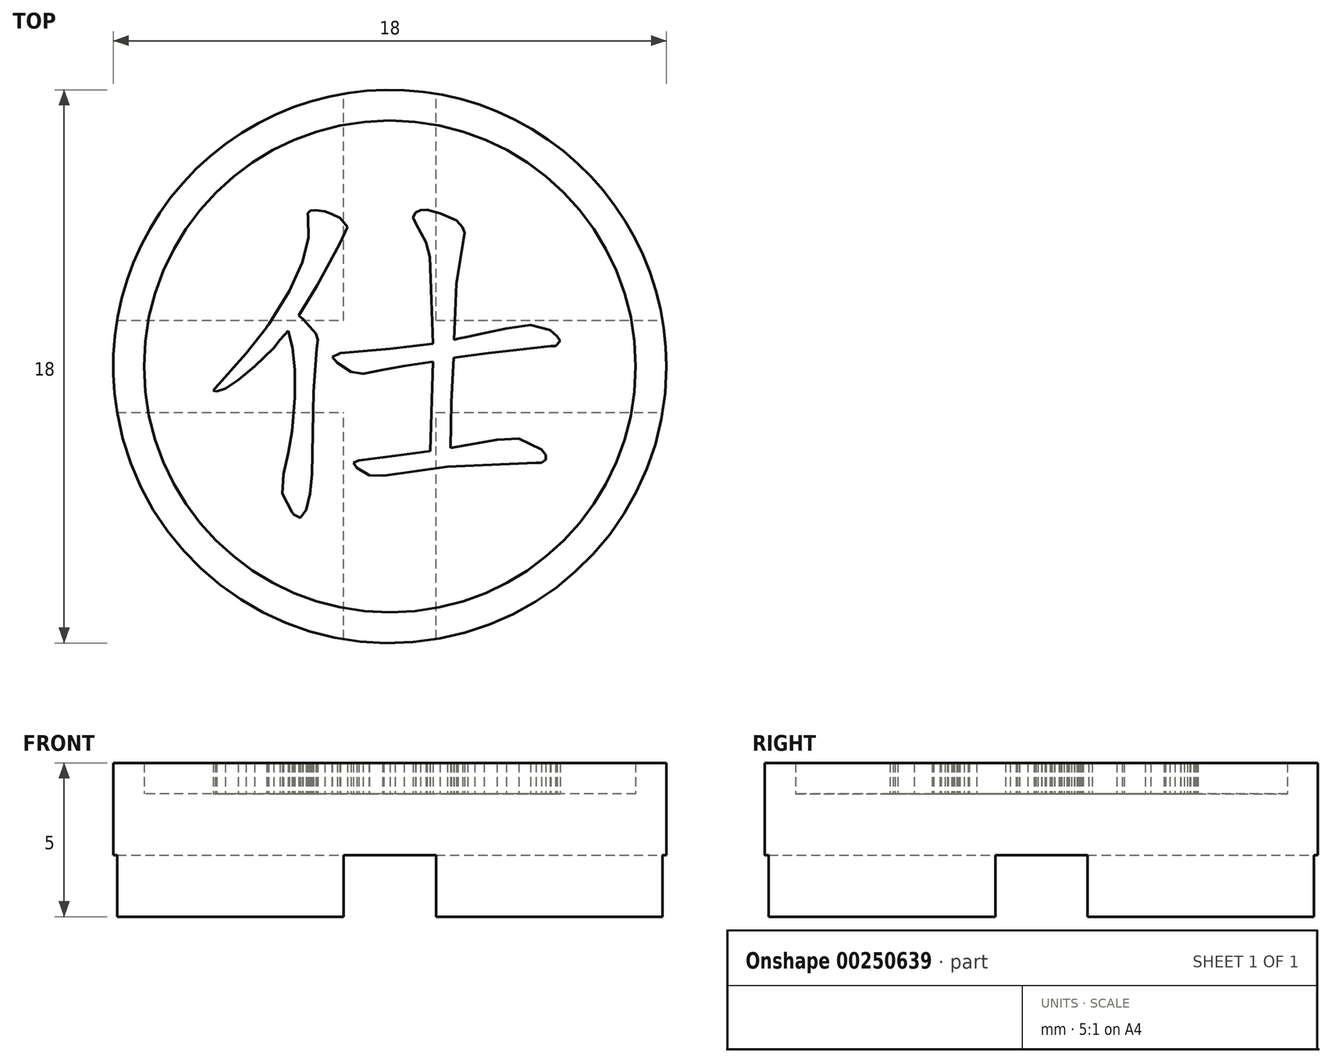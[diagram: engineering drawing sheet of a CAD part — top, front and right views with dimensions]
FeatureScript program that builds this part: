
annotation { "Feature Type Name" : "Feature", "Feature Type Description" : "" }
export const myFeature = defineFeature(function(context is Context, id is Id, definition is map)
    precondition{}
    {
        {
            var Q0;
            Q0=qCreatedBy(makeId("Top.planeOp"),FACE);
            var sketch = newSketch(context, id + "F0", { "sketchPlane" : qUnion([Q0])});
            skCircle(sketch, "E0", {"center": v(-31.33, 19.76) * mm, "radius": 9 * mm});
            skSolve(sketch);
        }
        {
            var Q0;
            Q0=qSketchRegion(id+"F0",true);
            extrude(context, id + "F1", {"entities" : qUnion([Q0]), "depth" : 4 * mm});
        }
        {
            var Q0;
            Q0=makeQuery(id+"F1.opExtrude","CAP_FACE",FACE,{"disambiguationData":[OSD([sQuery(id+"F0.wireOp",EDGE,"E0")])],"isStart":false});
            var sketch = newSketch(context, id + "F2", { "sketchPlane" : qUnion([Q0])});
            skCircle(sketch, "E1", {"center": v(-31.33, 19.76) * mm, "radius": 8 * mm});
            skCircle(sketch, "E2", {"center": v(-31.33, 19.76) * mm, "radius": 9 * mm});
            skSolve(sketch);
        }
        {
            var Q0;
            Q0=makeQuery(id+"F1.opExtrude","CAP_FACE",FACE,{"disambiguationData":[OSD([sQuery(id+"F0.wireOp",EDGE,"E0")])],"isStart":true});
            var sketch = newSketch(context, id + "F3", { "sketchPlane" : qUnion([Q0])});
            skLineSegment(sketch, "E3", {"start": v(-31.33, -19.76) * mm, "end": v(-22.33, -19.76) * mm, "construction": true});
            skLineSegment(sketch, "E4", {"start": v(-31.33, -19.76) * mm, "end": v(-31.33, -10.76) * mm, "construction": true});
            skLineSegment(sketch, "E5", {"start": v(-31.33, -19.76) * mm, "end": v(-40.33, -19.76) * mm, "construction": true});
            skLineSegment(sketch, "E6", {"start": v(-31.33, -19.76) * mm, "end": v(-31.33, -28.76) * mm, "construction": true});
            skLineSegment(sketch, "E7.bottom", {"start": v(-40.33, -28.76) * mm, "end": v(-22.33, -28.76) * mm});
            skLineSegment(sketch, "E7.top", {"start": v(-40.33, -10.76) * mm, "end": v(-22.33, -10.76) * mm});
            skLineSegment(sketch, "E7.left", {"start": v(-22.33, -10.76) * mm, "end": v(-22.33, -28.76) * mm});
            skLineSegment(sketch, "E7.right", {"start": v(-40.33, -10.76) * mm, "end": v(-40.33, -28.76) * mm});
            skPoint(sketch, "E8", {"position": v(-31.33, -28.76) * mm});
            skPoint(sketch, "E9", {"position": v(-40.33, -19.76) * mm});
            skPoint(sketch, "E10", {"position": v(-22.33, -19.76) * mm});
            skPoint(sketch, "E11", {"position": v(-31.33, -10.76) * mm});
            skLineSegment(sketch, "E12.bottom", {"start": v(-32.83, -10.76) * mm, "end": v(-29.83, -10.76) * mm});
            skLineSegment(sketch, "E12.top", {"start": v(-32.83, -28.76) * mm, "end": v(-29.83, -28.76) * mm});
            skLineSegment(sketch, "E12.left", {"start": v(-32.83, -10.76) * mm, "end": v(-32.83, -28.76) * mm});
            skLineSegment(sketch, "E12.right", {"start": v(-29.83, -10.76) * mm, "end": v(-29.83, -28.76) * mm});
            skLineSegment(sketch, "E13.bottom", {"start": v(-40.33, -18.26) * mm, "end": v(-22.33, -18.26) * mm});
            skLineSegment(sketch, "E13.top", {"start": v(-40.33, -21.26) * mm, "end": v(-22.33, -21.26) * mm});
            skLineSegment(sketch, "E13.left", {"start": v(-40.33, -18.26) * mm, "end": v(-40.33, -21.26) * mm});
            skLineSegment(sketch, "E13.right", {"start": v(-22.33, -18.26) * mm, "end": v(-22.33, -21.26) * mm});
            skSolve(sketch);
        }
        {
            var Q0;
            {var subQ1=sQuery(id+"F3.wireOp",EDGE,"E12.bottom");var subQ3=makeQuery(id+"F1.opExtrude","CAP_EDGE",EDGE,{"disambiguationData":[OSD([sQuery(id+"F0.wireOp",EDGE,"E0")])],"isStart":true});var subQ4=makeQuery(id+"F3.imprint","INTERSECT",VERTEX,{"derivedFrom":[subQ3,subQ1]});Q0=makeQuery(id+"F3.imprint","IMPRINT",FACE,{"disambiguationData":[TD([[makeQuery(id+"F3.imprint","IMPRINT",EDGE,{"disambiguationData":[TD([[subQ4,1.0]])],"derivedFrom":subQ3}),1.0]])]});}
            var Q1;
            {var subQ1=sQuery(id+"F3.wireOp",EDGE,"E12.bottom");var subQ3=makeQuery(id+"F1.opExtrude","CAP_EDGE",EDGE,{"disambiguationData":[OSD([sQuery(id+"F0.wireOp",EDGE,"E0")])],"isStart":true});var subQ4=makeQuery(id+"F3.imprint","INTERSECT",VERTEX,{"derivedFrom":[subQ3,subQ1]});Q1=makeQuery(id+"F3.imprint","IMPRINT",FACE,{"disambiguationData":[TD([[makeQuery(id+"F3.imprint","IMPRINT",EDGE,{"disambiguationData":[TD([[subQ4,-1.0]])],"derivedFrom":subQ3}),1.0]])]});}
            var Q2;
            {var subQ1=sQuery(id+"F3.wireOp",EDGE,"E12.top");var subQ3=makeQuery(id+"F1.opExtrude","CAP_EDGE",EDGE,{"disambiguationData":[OSD([sQuery(id+"F0.wireOp",EDGE,"E0")])],"isStart":true});var subQ4=makeQuery(id+"F3.imprint","INTERSECT",VERTEX,{"derivedFrom":[subQ3,subQ1]});Q2=makeQuery(id+"F3.imprint","IMPRINT",FACE,{"disambiguationData":[TD([[makeQuery(id+"F3.imprint","IMPRINT",EDGE,{"disambiguationData":[TD([[subQ4,-1.0]])],"derivedFrom":subQ3}),1.0]])]});}
            var Q3;
            {var subQ1=sQuery(id+"F3.wireOp",EDGE,"E12.top");var subQ3=makeQuery(id+"F1.opExtrude","CAP_EDGE",EDGE,{"disambiguationData":[OSD([sQuery(id+"F0.wireOp",EDGE,"E0")])],"isStart":true});var subQ4=makeQuery(id+"F3.imprint","INTERSECT",VERTEX,{"derivedFrom":[subQ3,subQ1]});Q3=makeQuery(id+"F3.imprint","IMPRINT",FACE,{"disambiguationData":[TD([[makeQuery(id+"F3.imprint","IMPRINT",EDGE,{"disambiguationData":[TD([[subQ4,1.0]])],"derivedFrom":subQ3}),1.0]])]});}
            var Q4;
            {var subQ0=sQuery(id+"F3.wireOp",EDGE,"E13.left");var subQ3=makeQuery(id+"F1.opExtrude","CAP_EDGE",EDGE,{"disambiguationData":[OSD([sQuery(id+"F0.wireOp",EDGE,"E0")])],"isStart":true});var subQ5=makeQuery(id+"F3.imprint","INTERSECT",VERTEX,{"derivedFrom":[subQ3,subQ0]});Q4=makeQuery(id+"F3.imprint","IMPRINT",FACE,{"disambiguationData":[TD([[makeQuery(id+"F3.imprint","IMPRINT",EDGE,{"disambiguationData":[TD([[subQ5,-1.0]])],"derivedFrom":subQ3}),1.0]])]});}
            var Q5;
            {var subQ0=sQuery(id+"F3.wireOp",EDGE,"E13.right");var subQ3=makeQuery(id+"F1.opExtrude","CAP_EDGE",EDGE,{"disambiguationData":[OSD([sQuery(id+"F0.wireOp",EDGE,"E0")])],"isStart":true});var subQ5=makeQuery(id+"F3.imprint","INTERSECT",VERTEX,{"derivedFrom":[subQ3,subQ0]});Q5=makeQuery(id+"F3.imprint","IMPRINT",FACE,{"disambiguationData":[TD([[makeQuery(id+"F3.imprint","IMPRINT",EDGE,{"disambiguationData":[TD([[subQ5,1.0]])],"derivedFrom":subQ3}),1.0]])]});}
            var Q6;
            {var subQ0=sQuery(id+"F3.wireOp",EDGE,"E13.left");var subQ3=makeQuery(id+"F1.opExtrude","CAP_EDGE",EDGE,{"disambiguationData":[OSD([sQuery(id+"F0.wireOp",EDGE,"E0")])],"isStart":true});var subQ5=makeQuery(id+"F3.imprint","INTERSECT",VERTEX,{"derivedFrom":[subQ3,subQ0]});Q6=makeQuery(id+"F3.imprint","IMPRINT",FACE,{"disambiguationData":[TD([[makeQuery(id+"F3.imprint","IMPRINT",EDGE,{"disambiguationData":[TD([[subQ5,1.0]])],"derivedFrom":subQ3}),1.0]])]});}
            var Q7;
            {var subQ0=sQuery(id+"F3.wireOp",EDGE,"E13.right");var subQ3=makeQuery(id+"F1.opExtrude","CAP_EDGE",EDGE,{"disambiguationData":[OSD([sQuery(id+"F0.wireOp",EDGE,"E0")])],"isStart":true});var subQ5=makeQuery(id+"F3.imprint","INTERSECT",VERTEX,{"derivedFrom":[subQ3,subQ0]});Q7=makeQuery(id+"F3.imprint","IMPRINT",FACE,{"disambiguationData":[TD([[makeQuery(id+"F3.imprint","IMPRINT",EDGE,{"disambiguationData":[TD([[subQ5,-1.0]])],"derivedFrom":subQ3}),1.0]])]});}
            var Q8;
            {var subQ3=makeQuery(id+"F1.opExtrude","CAP_EDGE",EDGE,{"disambiguationData":[OSD([sQuery(id+"F0.wireOp",EDGE,"E0")])],"isStart":true});var subQ5=sQuery(id+"F3.wireOp",EDGE,"E12.left");var subQ8=makeQuery(id+"F3.imprint","INTERSECT",VERTEX,{"disambiguationData":[OD(1.0)],"derivedFrom":[subQ3,subQ5]});Q8=makeQuery(id+"F3.imprint","IMPRINT",FACE,{"disambiguationData":[TD([[makeQuery(id+"F3.imprint","IMPRINT",EDGE,{"disambiguationData":[TD([[subQ8,-1.0]])],"derivedFrom":subQ3}),1.0]])]});}
            var Q9;
            {var subQ3=makeQuery(id+"F1.opExtrude","CAP_EDGE",EDGE,{"disambiguationData":[OSD([sQuery(id+"F0.wireOp",EDGE,"E0")])],"isStart":true});var subQ5=sQuery(id+"F3.wireOp",EDGE,"E12.right");var subQ8=makeQuery(id+"F3.imprint","INTERSECT",VERTEX,{"disambiguationData":[OD(1.0)],"derivedFrom":[subQ3,subQ5]});Q9=makeQuery(id+"F3.imprint","IMPRINT",FACE,{"disambiguationData":[TD([[makeQuery(id+"F3.imprint","IMPRINT",EDGE,{"disambiguationData":[TD([[subQ8,1.0]])],"derivedFrom":subQ3}),1.0]])]});}
            var Q10;
            {var subQ3=makeQuery(id+"F1.opExtrude","CAP_EDGE",EDGE,{"disambiguationData":[OSD([sQuery(id+"F0.wireOp",EDGE,"E0")])],"isStart":true});var subQ5=sQuery(id+"F3.wireOp",EDGE,"E12.left");var subQ8=makeQuery(id+"F3.imprint","INTERSECT",VERTEX,{"disambiguationData":[OD(0.0)],"derivedFrom":[subQ3,subQ5]});Q10=makeQuery(id+"F3.imprint","IMPRINT",FACE,{"disambiguationData":[TD([[makeQuery(id+"F3.imprint","IMPRINT",EDGE,{"disambiguationData":[TD([[subQ8,1.0]])],"derivedFrom":subQ3}),1.0]])]});}
            var Q11;
            {var subQ3=makeQuery(id+"F1.opExtrude","CAP_EDGE",EDGE,{"disambiguationData":[OSD([sQuery(id+"F0.wireOp",EDGE,"E0")])],"isStart":true});var subQ5=sQuery(id+"F3.wireOp",EDGE,"E12.right");var subQ8=makeQuery(id+"F3.imprint","INTERSECT",VERTEX,{"disambiguationData":[OD(0.0)],"derivedFrom":[subQ3,subQ5]});Q11=makeQuery(id+"F3.imprint","IMPRINT",FACE,{"disambiguationData":[TD([[makeQuery(id+"F3.imprint","IMPRINT",EDGE,{"disambiguationData":[TD([[subQ8,-1.0]])],"derivedFrom":subQ3}),1.0]])]});}
            var Q12;
            {var subQ2=sQuery(id+"F3.wireOp",EDGE,"E12.left");var subQ4=sQuery(id+"F3.wireOp",EDGE,"E13.bottom");var subQ8=makeQuery(id+"F3.imprint","INTERSECT",VERTEX,{"derivedFrom":[subQ2,subQ4]});Q12=makeQuery(id+"F3.imprint","IMPRINT",FACE,{"disambiguationData":[TD([[makeQuery(id+"F3.imprint","IMPRINT",EDGE,{"disambiguationData":[TD([[subQ8,1.0]])],"derivedFrom":subQ2}),1.0]])]});}
            var Q13;
            {var subQ1=sQuery(id+"F3.wireOp",EDGE,"E12.left");var subQ5=sQuery(id+"F3.wireOp",EDGE,"E13.bottom");var subQ6=makeQuery(id+"F3.imprint","INTERSECT",VERTEX,{"derivedFrom":[subQ1,subQ5]});Q13=makeQuery(id+"F3.imprint","IMPRINT",FACE,{"disambiguationData":[TD([[makeQuery(id+"F3.imprint","IMPRINT",EDGE,{"disambiguationData":[TD([[subQ6,-1.0]])],"derivedFrom":subQ1}),-1.0]])]});}
            var Q14;
            {var subQ0=sQuery(id+"F3.wireOp",EDGE,"E13.top");var subQ1=sQuery(id+"F3.wireOp",EDGE,"E12.left");var subQ2=makeQuery(id+"F3.imprint","INTERSECT",VERTEX,{"derivedFrom":[subQ1,subQ0]});Q14=makeQuery(id+"F3.imprint","IMPRINT",FACE,{"disambiguationData":[TD([[makeQuery(id+"F3.imprint","IMPRINT",EDGE,{"disambiguationData":[TD([[subQ2,-1.0]])],"derivedFrom":subQ1}),1.0]])]});}
            var Q15;
            {var subQ2=sQuery(id+"F3.wireOp",EDGE,"E13.bottom");var subQ5=sQuery(id+"F3.wireOp",EDGE,"E12.right");var subQ8=makeQuery(id+"F3.imprint","INTERSECT",VERTEX,{"derivedFrom":[subQ5,subQ2]});Q15=makeQuery(id+"F3.imprint","IMPRINT",FACE,{"disambiguationData":[TD([[makeQuery(id+"F3.imprint","IMPRINT",EDGE,{"disambiguationData":[TD([[subQ8,-1.0]])],"derivedFrom":subQ5}),1.0]])]});}
            var Q16;
            {var subQ0=sQuery(id+"F3.wireOp",EDGE,"E13.bottom");var subQ1=sQuery(id+"F3.wireOp",EDGE,"E12.left");var subQ2=makeQuery(id+"F3.imprint","INTERSECT",VERTEX,{"derivedFrom":[subQ1,subQ0]});Q16=makeQuery(id+"F3.imprint","IMPRINT",FACE,{"disambiguationData":[TD([[makeQuery(id+"F3.imprint","IMPRINT",EDGE,{"disambiguationData":[TD([[subQ2,-1.0]])],"derivedFrom":subQ1}),1.0]])]});}
            extrude(context, id + "F4", {"entities" : qUnion([Q0, Q1, Q2, Q3, Q4, Q5, Q6, Q7, Q8, Q9, Q10, Q11, Q12, Q13, Q14, Q15, Q16]), "operationType" : NewBodyOperationType.REMOVE, "oppositeDirection" : true, "depth" : 2 * mm});
        }
        {
            var Q0;
            Q0=qSketchRegion(id+"F2",true);
            var Q1;
            Q1=makeQuery(id+"F2.imprint","IMPRINT",FACE,{"disambiguationData":[TD([[makeQuery(id+"F2.imprint","IMPRINT",EDGE,{"derivedFrom":sQuery(id+"F2.wireOp",EDGE,"hKqnuJLd-dfdz-vJIs-yDKo-c4hLNRw30SuP")}),-1.0]])]});
            extrude(context, id + "F5", {"entities" : qUnion([Q0, Q1]), "operationType" : NewBodyOperationType.ADD, "depth" : 1 * mm});
        }
        {
            var Q0;
            Q0=makeQuery(id+"F1.opExtrude","CAP_FACE",FACE,{"disambiguationData":[OSD([sQuery(id+"F0.wireOp",EDGE,"E0")])],"isStart":false});
            var sketch = newSketch(context, id + "F6", { "sketchPlane" : qUnion([Q0])});
            skLineSegment(sketch, "E14", {"start": v(-34.64, 20.92) * mm, "end": v(-34.5, 20.37) * mm});
            skLineSegment(sketch, "E15", {"start": v(-34.5, 20.37) * mm, "end": v(-34.42, 19.65) * mm});
            skLineSegment(sketch, "E16", {"start": v(-34.42, 19.65) * mm, "end": v(-34.42, 18.74) * mm});
            skLineSegment(sketch, "E17", {"start": v(-34.42, 18.74) * mm, "end": v(-34.51, 17.65) * mm});
            skLineSegment(sketch, "E18", {"start": v(-34.51, 17.65) * mm, "end": v(-34.64, 16.93) * mm});
            skLineSegment(sketch, "E19", {"start": v(-34.64, 16.93) * mm, "end": v(-34.8, 16.25) * mm});
            skLineSegment(sketch, "E20", {"start": v(-34.8, 16.25) * mm, "end": v(-34.83, 15.62) * mm});
            skLineSegment(sketch, "E21", {"start": v(-34.83, 15.62) * mm, "end": v(-34.51, 15) * mm});
            skLineSegment(sketch, "E22", {"start": v(-34.51, 15) * mm, "end": v(-34.45, 14.93) * mm});
            skLineSegment(sketch, "E23", {"start": v(-34.45, 14.93) * mm, "end": v(-34.25, 14.84) * mm});
            skLineSegment(sketch, "E24", {"start": v(-34.25, 14.84) * mm, "end": v(-34.05, 15.09) * mm});
            skLineSegment(sketch, "E25", {"start": v(-34.05, 15.09) * mm, "end": v(-33.92, 15.62) * mm});
            skLineSegment(sketch, "E26", {"start": v(-33.92, 15.62) * mm, "end": v(-33.86, 16.24) * mm});
            skLineSegment(sketch, "E27", {"start": v(-33.86, 16.24) * mm, "end": v(-33.82, 18.93) * mm});
            skLineSegment(sketch, "E28", {"start": v(-33.82, 18.93) * mm, "end": v(-33.7, 20.33) * mm});
            skLineSegment(sketch, "E29", {"start": v(-33.7, 20.33) * mm, "end": v(-33.68, 20.63) * mm});
            skLineSegment(sketch, "E30", {"start": v(-33.68, 20.63) * mm, "end": v(-33.74, 20.83) * mm});
            skLineSegment(sketch, "E31", {"start": v(-33.74, 20.83) * mm, "end": v(-34.15, 21.3) * mm});
            skLineSegment(sketch, "E32", {"start": v(-34.15, 21.3) * mm, "end": v(-34.3, 21.41) * mm});
            skLineSegment(sketch, "E33", {"start": v(-34.3, 21.41) * mm, "end": v(-33.7, 22.39) * mm});
            skLineSegment(sketch, "E34", {"start": v(-33.7, 22.39) * mm, "end": v(-32.96, 23.76) * mm});
            skLineSegment(sketch, "E35", {"start": v(-32.96, 23.76) * mm, "end": v(-32.78, 24.12) * mm});
            skLineSegment(sketch, "E36", {"start": v(-32.78, 24.12) * mm, "end": v(-32.7, 24.3) * mm});
            skLineSegment(sketch, "E37", {"start": v(-32.7, 24.3) * mm, "end": v(-32.95, 24.59) * mm});
            skLineSegment(sketch, "E38", {"start": v(-32.95, 24.59) * mm, "end": v(-33.21, 24.71) * mm});
            skLineSegment(sketch, "E39", {"start": v(-33.21, 24.71) * mm, "end": v(-33.45, 24.8) * mm});
            skLineSegment(sketch, "E40", {"start": v(-33.45, 24.8) * mm, "end": v(-33.73, 24.84) * mm});
            skLineSegment(sketch, "E41", {"start": v(-33.73, 24.84) * mm, "end": v(-33.91, 24.84) * mm});
            skLineSegment(sketch, "E42", {"start": v(-33.91, 24.84) * mm, "end": v(-34, 24.74) * mm});
            skLineSegment(sketch, "E43", {"start": v(-34, 24.74) * mm, "end": v(-33.99, 24.62) * mm});
            skLineSegment(sketch, "E44", {"start": v(-33.99, 24.62) * mm, "end": v(-33.98, 23.95) * mm});
            skLineSegment(sketch, "E45", {"start": v(-33.98, 23.95) * mm, "end": v(-34.18, 23.15) * mm});
            skLineSegment(sketch, "E46", {"start": v(-34.18, 23.15) * mm, "end": v(-34.6, 22.2) * mm});
            skLineSegment(sketch, "E47", {"start": v(-34.6, 22.2) * mm, "end": v(-35.27, 21.12) * mm});
            skLineSegment(sketch, "E48", {"start": v(-35.27, 21.12) * mm, "end": v(-35.33, 21.07) * mm});
            skLineSegment(sketch, "E49", {"start": v(-35.33, 21.07) * mm, "end": v(-35.34, 21.03) * mm});
            skLineSegment(sketch, "E50", {"start": v(-35.34, 21.03) * mm, "end": v(-36, 20.18) * mm});
            skLineSegment(sketch, "E51", {"start": v(-36, 20.18) * mm, "end": v(-37.01, 19.05) * mm});
            skLineSegment(sketch, "E52", {"start": v(-37.01, 19.05) * mm, "end": v(-37.08, 18.97) * mm});
            skLineSegment(sketch, "E53", {"start": v(-37.08, 18.97) * mm, "end": v(-36.96, 18.95) * mm});
            skLineSegment(sketch, "E54", {"start": v(-36.96, 18.95) * mm, "end": v(-36.68, 19.04) * mm});
            skLineSegment(sketch, "E55", {"start": v(-36.68, 19.04) * mm, "end": v(-36.27, 19.31) * mm});
            skLineSegment(sketch, "E56", {"start": v(-36.27, 19.31) * mm, "end": v(-35.74, 19.76) * mm});
            skLineSegment(sketch, "E57", {"start": v(-35.74, 19.76) * mm, "end": v(-35.1, 20.36) * mm});
            skLineSegment(sketch, "E58", {"start": v(-35.1, 20.36) * mm, "end": v(-34.9, 20.62) * mm});
            skLineSegment(sketch, "E59", {"start": v(-34.9, 20.62) * mm, "end": v(-34.64, 20.92) * mm});
            skLineSegment(sketch, "E60", {"start": v(-30.01, 17) * mm, "end": v(-31.16, 16.85) * mm});
            skLineSegment(sketch, "E61", {"start": v(-31.16, 16.85) * mm, "end": v(-32.35, 16.7) * mm});
            skLineSegment(sketch, "E62", {"start": v(-32.35, 16.7) * mm, "end": v(-32.51, 16.63) * mm});
            skLineSegment(sketch, "E63", {"start": v(-32.51, 16.63) * mm, "end": v(-32.4, 16.46) * mm});
            skLineSegment(sketch, "E64", {"start": v(-32.4, 16.46) * mm, "end": v(-32, 16.22) * mm});
            skLineSegment(sketch, "E65", {"start": v(-32, 16.22) * mm, "end": v(-31.52, 16.2) * mm});
            skLineSegment(sketch, "E66", {"start": v(-31.52, 16.2) * mm, "end": v(-29.46, 16.5) * mm});
            skLineSegment(sketch, "E67", {"start": v(-29.46, 16.5) * mm, "end": v(-26.57, 16.63) * mm});
            skLineSegment(sketch, "E68", {"start": v(-26.57, 16.63) * mm, "end": v(-26.4, 16.63) * mm});
            skLineSegment(sketch, "E69", {"start": v(-26.4, 16.63) * mm, "end": v(-26.25, 16.73) * mm});
            skLineSegment(sketch, "E70", {"start": v(-26.25, 16.73) * mm, "end": v(-26.26, 16.88) * mm});
            skLineSegment(sketch, "E71", {"start": v(-26.26, 16.88) * mm, "end": v(-26.4, 17.06) * mm});
            skLineSegment(sketch, "E72", {"start": v(-26.4, 17.06) * mm, "end": v(-27.13, 17.4) * mm});
            skLineSegment(sketch, "E73", {"start": v(-27.13, 17.4) * mm, "end": v(-27.84, 17.38) * mm});
            skLineSegment(sketch, "E74", {"start": v(-27.84, 17.38) * mm, "end": v(-28.56, 17.24) * mm});
            skLineSegment(sketch, "E75", {"start": v(-28.56, 17.24) * mm, "end": v(-29.36, 17.11) * mm});
            skLineSegment(sketch, "E76", {"start": v(-29.36, 17.11) * mm, "end": v(-29.33, 18.6) * mm});
            skLineSegment(sketch, "E77", {"start": v(-29.33, 18.6) * mm, "end": v(-29.26, 20.04) * mm});
            skLineSegment(sketch, "E78", {"start": v(-29.26, 20.04) * mm, "end": v(-28.8, 20.1) * mm});
            skLineSegment(sketch, "E79", {"start": v(-28.8, 20.1) * mm, "end": v(-28.12, 20.19) * mm});
            skLineSegment(sketch, "E80", {"start": v(-28.12, 20.19) * mm, "end": v(-27.21, 20.3) * mm});
            skLineSegment(sketch, "E81", {"start": v(-27.21, 20.3) * mm, "end": v(-26.09, 20.42) * mm});
            skLineSegment(sketch, "E82", {"start": v(-26.09, 20.42) * mm, "end": v(-25.94, 20.42) * mm});
            skLineSegment(sketch, "E83", {"start": v(-25.94, 20.42) * mm, "end": v(-25.8, 20.59) * mm});
            skLineSegment(sketch, "E84", {"start": v(-25.8, 20.59) * mm, "end": v(-25.88, 20.74) * mm});
            skLineSegment(sketch, "E85", {"start": v(-25.88, 20.74) * mm, "end": v(-26.11, 20.94) * mm});
            skLineSegment(sketch, "E86", {"start": v(-26.11, 20.94) * mm, "end": v(-26.75, 21.1) * mm});
            skLineSegment(sketch, "E87", {"start": v(-26.75, 21.1) * mm, "end": v(-27.54, 21) * mm});
            skLineSegment(sketch, "E88", {"start": v(-27.54, 21) * mm, "end": v(-28.27, 20.84) * mm});
            skLineSegment(sketch, "E89", {"start": v(-28.27, 20.84) * mm, "end": v(-28.79, 20.73) * mm});
            skLineSegment(sketch, "E90", {"start": v(-28.79, 20.73) * mm, "end": v(-29.11, 20.67) * mm});
            skLineSegment(sketch, "E91", {"start": v(-29.11, 20.67) * mm, "end": v(-29.24, 20.63) * mm});
            skLineSegment(sketch, "E92", {"start": v(-29.24, 20.63) * mm, "end": v(-29.17, 22.45) * mm});
            skLineSegment(sketch, "E93", {"start": v(-29.17, 22.45) * mm, "end": v(-28.9, 24.1) * mm});
            skLineSegment(sketch, "E94", {"start": v(-28.9, 24.1) * mm, "end": v(-28.96, 24.28) * mm});
            skLineSegment(sketch, "E95", {"start": v(-28.96, 24.28) * mm, "end": v(-29.17, 24.51) * mm});
            skLineSegment(sketch, "E96", {"start": v(-29.17, 24.51) * mm, "end": v(-29.7, 24.74) * mm});
            skLineSegment(sketch, "E97", {"start": v(-29.7, 24.74) * mm, "end": v(-30.11, 24.86) * mm});
            skLineSegment(sketch, "E98", {"start": v(-30.11, 24.86) * mm, "end": v(-30.34, 24.84) * mm});
            skLineSegment(sketch, "E99", {"start": v(-30.34, 24.84) * mm, "end": v(-30.5, 24.77) * mm});
            skLineSegment(sketch, "E100", {"start": v(-30.5, 24.77) * mm, "end": v(-30.57, 24.6) * mm});
            skLineSegment(sketch, "E101", {"start": v(-30.57, 24.6) * mm, "end": v(-30.48, 24.41) * mm});
            skLineSegment(sketch, "E102", {"start": v(-30.48, 24.41) * mm, "end": v(-30.15, 23.8) * mm});
            skLineSegment(sketch, "E103", {"start": v(-30.15, 23.8) * mm, "end": v(-30.02, 23.32) * mm});
            skLineSegment(sketch, "E104", {"start": v(-30.02, 23.32) * mm, "end": v(-29.98, 21.92) * mm});
            skLineSegment(sketch, "E105", {"start": v(-29.98, 21.92) * mm, "end": v(-29.93, 20.5) * mm});
            skLineSegment(sketch, "E106", {"start": v(-29.93, 20.5) * mm, "end": v(-31.32, 20.33) * mm});
            skLineSegment(sketch, "E107", {"start": v(-31.32, 20.33) * mm, "end": v(-32.93, 20.2) * mm});
            skLineSegment(sketch, "E108", {"start": v(-32.93, 20.2) * mm, "end": v(-33.2, 20.06) * mm});
            skLineSegment(sketch, "E109", {"start": v(-33.2, 20.06) * mm, "end": v(-33.04, 19.87) * mm});
            skLineSegment(sketch, "E110", {"start": v(-33.04, 19.87) * mm, "end": v(-32.6, 19.58) * mm});
            skLineSegment(sketch, "E111", {"start": v(-32.6, 19.58) * mm, "end": v(-32.2, 19.52) * mm});
            skLineSegment(sketch, "E112", {"start": v(-32.2, 19.52) * mm, "end": v(-32.01, 19.56) * mm});
            skLineSegment(sketch, "E113", {"start": v(-32.01, 19.56) * mm, "end": v(-31.56, 19.65) * mm});
            skLineSegment(sketch, "E114", {"start": v(-31.56, 19.65) * mm, "end": v(-30.87, 19.77) * mm});
            skLineSegment(sketch, "E115", {"start": v(-30.87, 19.77) * mm, "end": v(-29.93, 19.92) * mm});
            skLineSegment(sketch, "E116", {"start": v(-29.93, 19.92) * mm, "end": v(-30.01, 17) * mm});
            skSolve(sketch);
        }
        {
            var Q0;
            Q0 = qSketchRegion(id + "F6", true);
            extrude(context, id + "F7", {"entities" : qUnion([Q0]), "operationType" : NewBodyOperationType.ADD, "depth" : 1 * mm, "offsetDistance" : 25 * mm});
        }
    });
